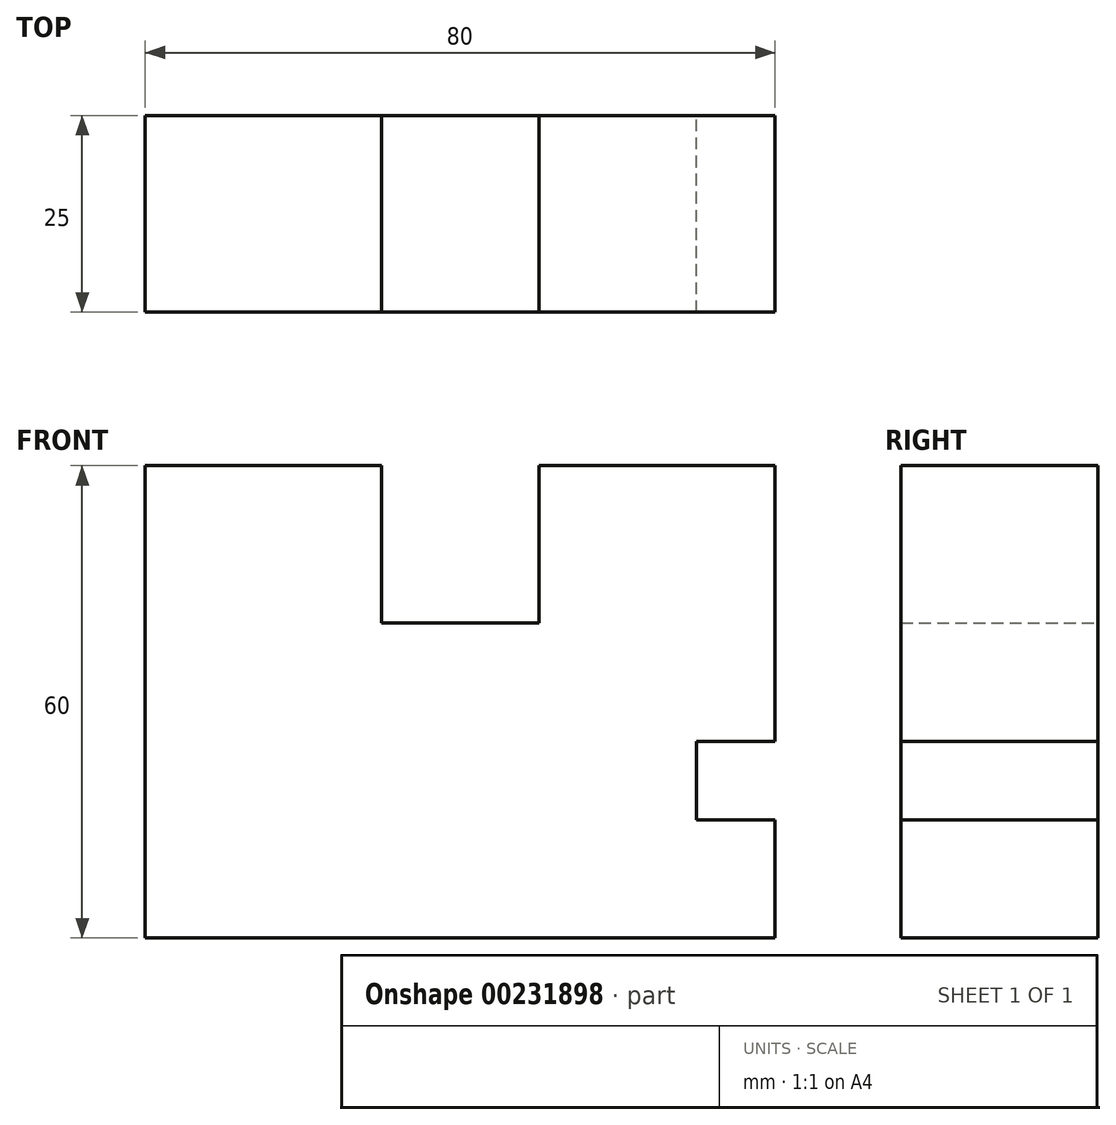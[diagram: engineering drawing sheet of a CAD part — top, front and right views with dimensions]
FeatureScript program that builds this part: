
annotation { "Feature Type Name" : "Feature", "Feature Type Description" : "" }
export const myFeature = defineFeature(function(context is Context, id is Id, definition is map)
    precondition{}
    {
        {
            var Q0;
            Q0=qCreatedBy(makeId("Front.planeOp"),FACE);
            var sketch = newSketch(context, id + "F0", { "sketchPlane" : qUnion([Q0])});
            skLineSegment(sketch, "E0", {"start": v(-30, 40) * mm, "end": v(-30, 60) * mm});
            skLineSegment(sketch, "E1", {"start": v(-30, 60) * mm, "end": v(0, 60) * mm});
            skLineSegment(sketch, "E2", {"start": v(0, 15) * mm, "end": v(0, 0) * mm});
            skLineSegment(sketch, "E3", {"start": v(-30, 40) * mm, "end": v(-50, 40) * mm});
            skLineSegment(sketch, "E4", {"start": v(-50, 40) * mm, "end": v(-50, 60) * mm});
            skLineSegment(sketch, "E5", {"start": v(-50, 60) * mm, "end": v(-80, 60) * mm});
            skLineSegment(sketch, "E6", {"start": v(-80, 60) * mm, "end": v(-80, 0) * mm});
            skLineSegment(sketch, "E7", {"start": v(-80, 0) * mm, "end": v(0, 0) * mm});
            skLineSegment(sketch, "E8", {"start": v(0, 60) * mm, "end": v(0, 25) * mm});
            skLineSegment(sketch, "E9", {"start": v(0, 25) * mm, "end": v(-10, 25) * mm});
            skLineSegment(sketch, "E10", {"start": v(-10, 25) * mm, "end": v(-10, 15) * mm});
            skLineSegment(sketch, "E11", {"start": v(-10, 15) * mm, "end": v(0, 15) * mm});
            skSolve(sketch);
        }
        {
            var Q0;
            Q0=makeQuery(id+"F0.imprint","IMPRINT",FACE,{"disambiguationData":[TD([[makeQuery(id+"F0.imprint","IMPRINT",EDGE,{"derivedFrom":sQuery(id+"F0.wireOp",EDGE,"E0")}),-1.0]])]});
            extrude(context, id + "F1", {"entities" : qUnion([Q0]), "depth" : 25 * mm});
        }
    });
